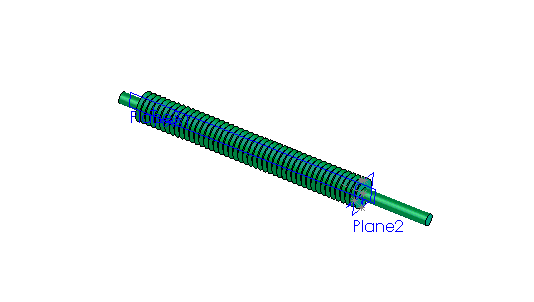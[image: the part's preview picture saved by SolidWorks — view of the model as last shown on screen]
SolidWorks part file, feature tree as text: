
SOLIDWORKS PART (.sldprt)
format: sldprt  version: not decoded by parser v0  size: 332,288 bytes
history: native  units: mm
features: sketch x5, extrude x3, plane x2, cut_revolve x1, pattern_linear x1 (+12 scaffold rows collapsed; 1 parser-record rows omitted)
feature tree (25):
  scaffold x12  (default folders/planes/origin — collapsed)
  parser-record x1  (decoder bookkeeping rows leaked as tree rows — omitted from the tree; the rows remain in map.json)
  sketch  "Sketch3"  dims[D1=7.9375mm]
  extrude  "Extrude1"  Depth=63.5mm
  sketch  "Sketch4"  dims[D1=3.175mm]
  extrude  "Extrude2"  Depth=6.35mm
  sketch  "Sketch5"  dims[D1=3.175mm]
  extrude  "Extrude3"  Depth=19.05mm
  plane  "Plane2"
  sketch  "Sketch6"
  plane  "Plane3"
  sketch  "Sketch7"  dims[D1=0.8636mm D2=1.4097mm D3=~0.70612mm D4=0.8636mm]
  cut_revolve  "Cut-Revolve1"  Angle=360deg
  pattern_linear  "LPattern1"  Count1=50 Count2=1 Spacing1=1.411224mm Spacing2=50mm
decode coverage: 9 of 10 modeling features carry decoded parameters
note: ~ marks probable driven/reference dimensions
note: suppression state not decoded; provenance and decode notes live in map.json
